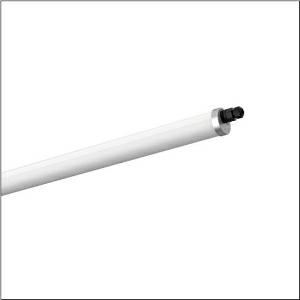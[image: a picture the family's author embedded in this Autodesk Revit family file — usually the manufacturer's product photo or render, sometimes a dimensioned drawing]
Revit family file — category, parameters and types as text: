
# Revit family: monsun_r__31_tube_51ft107n460a_2b58
name_source: partatom
category: Lighting Fixtures
units: mm (PartAtom-declared; Revit-internal decimal feet)

## family parameters
Cut with Voids When Loaded = No
Host = Face
Light Source = No
Part Type = Normal
Room Calculation Point = No
Round Connector Dimension = Use Diameter
Shared = No

## types (1)
- Monsun® 31 Tube (1 x LED, 6500 lm, 40 W, 4000K)
    Apparent Load = 40 VA
    CIE Flux Codes = 42 71 90 91 100
    Color Rendering = 80
    Color Temperature = 4000K
    Default Elevation = 1800 mm
    Description = Monsun® 31 Tube, tubular luminaire, primary optical cover: diffuser, of PMMA, light emission: direct distribution, primary light characteristic: symmetric, installation type: suspended mounting, surface-mounted, LED, rated luminous flux: 6.500lm, luminous efficacy: 160lm/W, light colour: 840, colour temperature: 4000K, with with 1 terminal, 3-pole, max. 2.5mm², through-wiring: 3x 1.5mm², mains connection: 220..240V, AC, 50/60Hz, rated input power: 41W, housing, cylindrical, of PMMA, semi-transparent, matt white, length: 1.560mm, diameter: 75mm, end cap, of stainless steel (V2A), protection rating (complete): IP67/IP69K, insulation class (complete): insulation class I (protective earthing), certification: CE, UKCA, impact resistance: IK07, permissible operating ambient temperature: -20..+40°C, corresponds to IFS (International Featured Standards) requirements for safety and quality in the food industry, packaging unit: 1 piece
    Height = 83 mm
    Lamp = 1 x LED
    Lamp Light Flux = 6500 lm
    Lamp Power = 40 W
    Lamp count = 1
    Length = 1560 mm
    Luminous efficacy = 163 lm/W
    Manufacturer = Siteco
    ModVariant = No
    Model = 51FT107N460A
    Mounting Place = Ceiling
    Mounting Type = Pendant
    Number of Poles = 1
    OnlyDefault = Yes
    Power Factor = 1
    Product Name = Monsun® 31 Tube
    Product group = tubular luminaire
    ProductGroupID = 907
    Protection Class = Protection class I
    RLX_Detail_Level = 1
    RlxData = <blob elided: 24821 chars, md5=727cfa8c>
    Socket = socket
    Standby Power = 0 W
    System Light Flux = 6500 lm
    System Power = 40 W
    Type Comments = Product without accessories
    Type Image = l_1228461.jpg
    URL = http://relux.com
    VarID = ---
    Voltage = 0 V
    Weight = 0.00 kg
    Width = 75 mm

## geometry (parser evidence)
native form markers: Blend x4, Sweep x12
no freeform markers — native parametric forms only
